# Revit family: CAME_КомплектКрепления_Створки_PSWLC
name_source: partatom
category: Специальное оборудование
units: mm (PartAtom-declared; Revit-internal decimal feet)

## family parameters
Всегда вертикально = Да
На основе рабочей плоскости = Нет
Общий = Да
При загрузке вырезать с полостями = Нет
Размер круглого соединителя = Использовать диаметр
Тип детали = Нормальный
Точка расчета площади = Нет

## types (1)
- PSWLC
    ADSK_URL документации изделия = https://camerussia.com
    ADSK_URL страницы изделия = https://camerussia.com
    ADSK_Версия Revit = 2019
    ADSK_Версия семейства = 1.0
    ADSK_Группирование = WING
    ADSK_Единица измерения = шт.
    ADSK_Завод-изготовитель = CAME
    ADSK_Код изделия = Код КСР 26.30.50.119.61.2.07.09
    ADSK_Количество = 1
    ADSK_Марка = АРТ: 001PSWLC
    ADSK_Масса = 2.76
    ADSK_Масса_Текст = 2.76
    ADSK_Наименование = Комплект крепления сторонней (дизайнерской) створки для WING 40
    ADSK_Наименование краткое = Комплект крепления дизайн. створки WING 40
    ADSK_Обозначение = ТУ 26.30.50-001-89603926-2021
    BL_BIM library = https://bimlib.pro
    URL = https://camerussia.com
    Группа модели = Турникеты
    Изготовитель = CAME
    Описание = Стальной зажим с уплотнителями для крепления самостоятельно изготовленной створки из стекла 8-10 мм. *доступно изготовление и поставка заказных створок — от 5 рабочих дней.
